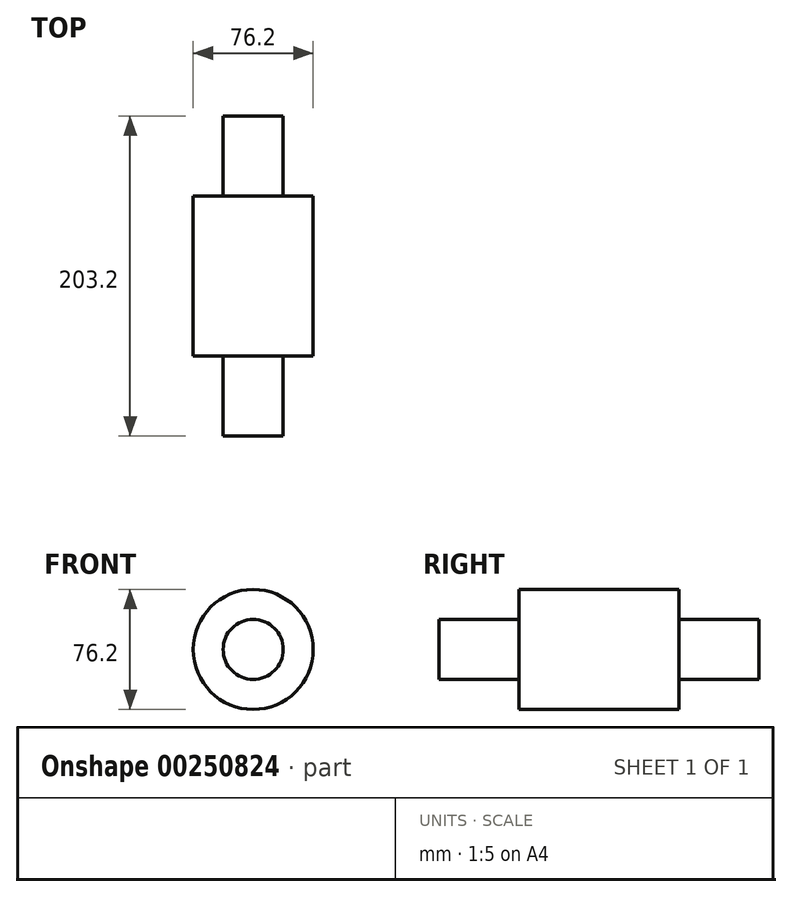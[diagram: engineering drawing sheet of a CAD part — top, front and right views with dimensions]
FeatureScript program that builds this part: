
annotation { "Feature Type Name" : "Feature", "Feature Type Description" : "" }
export const myFeature = defineFeature(function(context is Context, id is Id, definition is map)
    precondition{}
    {
        {
            var Q0;
            Q0=qCreatedBy(makeId("Front.planeOp"),FACE);
            var sketch = newSketch(context, id + "F0", { "sketchPlane" : qUnion([Q0])});
            skCircle(sketch, "E0", {"center": v(0, 0) * mm, "radius": 38.1 * mm});
            skSolve(sketch);
        }
        {
            var Q0;
            Q0=qCreatedBy(makeId("Front.planeOp"),FACE);
            var sketch = newSketch(context, id + "F1", { "sketchPlane" : qUnion([Q0])});
            skCircle(sketch, "E1", {"center": v(0, 0) * mm, "radius": 19.05 * mm});
            skSolve(sketch);
        }
        {
            var Q0;
            Q0 = qSketchRegion(id + "F1", true);
            extrude(context, id + "F2", {"entities" : qUnion([Q0]), "endBound" : BoundingType.SYMMETRIC, "depth" : 203.2 * mm});
        }
        {
            var Q0;
            Q0=makeQuery(id+"F0.imprint","IMPRINT",FACE,{"disambiguationData":[TD([[makeQuery(id+"F0.imprint","IMPRINT",EDGE,{"derivedFrom":sQuery(id+"F0.wireOp",EDGE,"E0")}),1.0]])]});
            extrude(context, id + "F3", {"entities" : qUnion([Q0]), "operationType" : NewBodyOperationType.ADD, "endBound" : BoundingType.SYMMETRIC, "depth" : 101.6 * mm});
        }
    });
